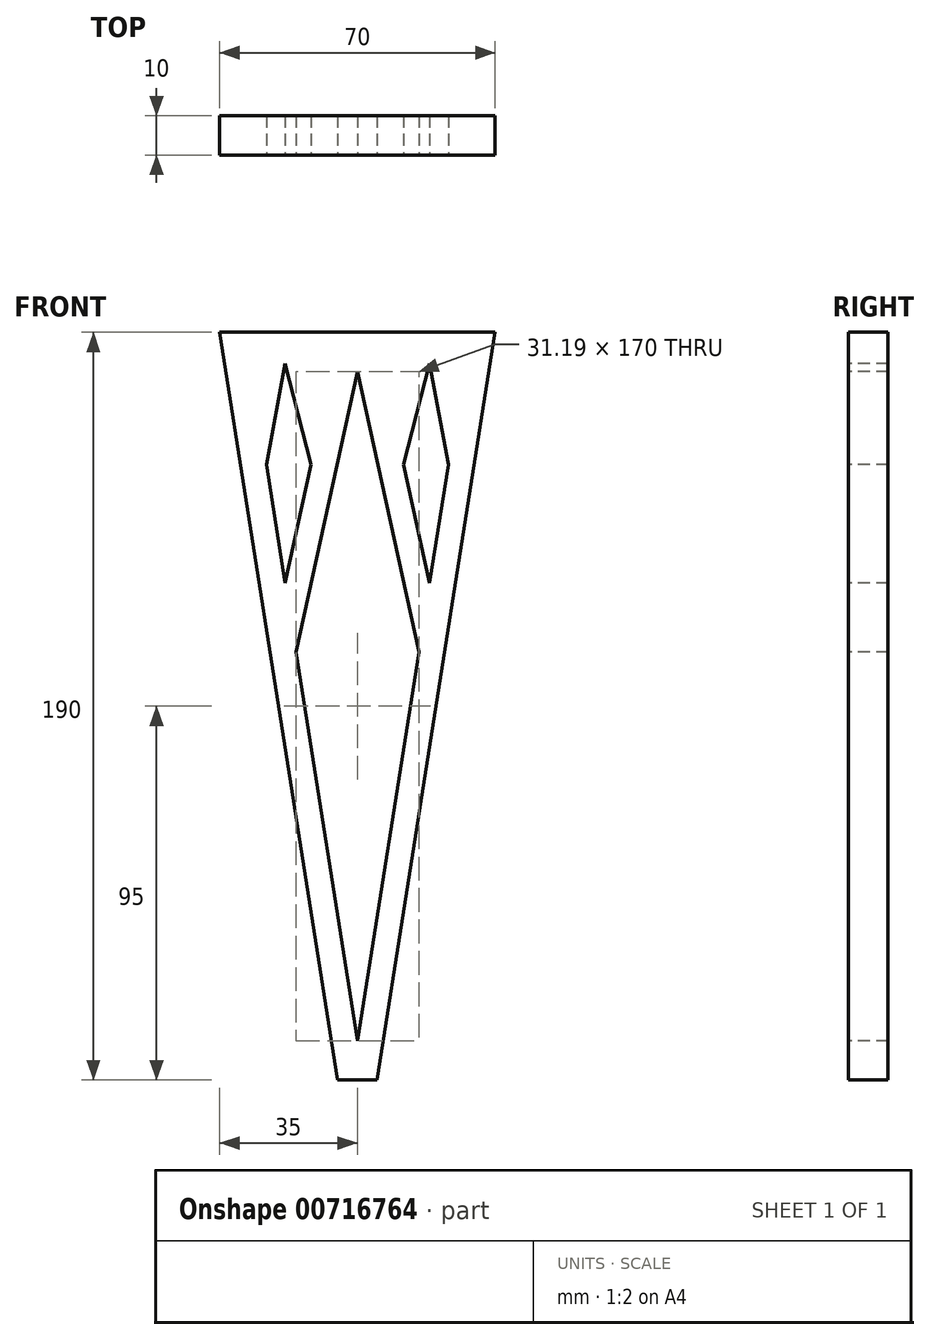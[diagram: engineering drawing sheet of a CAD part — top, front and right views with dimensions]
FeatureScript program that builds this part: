
annotation { "Feature Type Name" : "Feature", "Feature Type Description" : "" }
export const myFeature = defineFeature(function(context is Context, id is Id, definition is map)
    precondition{}
    {
        {
            var Q0;
            Q0=qCreatedBy(makeId("Top.planeOp"),FACE);
            var sketch = newSketch(context, id + "F0", { "sketchPlane" : qUnion([Q0])});
            skLineSegment(sketch, "E0.bottom", {"start": v(0, 0) * mm, "end": v(80, 0) * mm});
            skLineSegment(sketch, "E0.top", {"start": v(0, 16) * mm, "end": v(80, 16) * mm});
            skLineSegment(sketch, "E0.left", {"start": v(0, 0) * mm, "end": v(0, 16) * mm});
            skLineSegment(sketch, "E0.right", {"start": v(80, 0) * mm, "end": v(80, 16) * mm});
            skSolve(sketch);
        }
        {
            var Q0;
            Q0 = qSketchRegion(id + "F0", true);
            extrude(context, id + "F1", {"entities" : qUnion([Q0]), "depth" : 160 * mm, "offsetDistance" : 25 * mm});
        }
        {
            var Q0;
            Q0=makeQuery(id+"F1.opExtrude","SWEPT_FACE",FACE,{"disambiguationData":[OSD([sQuery(id+"F0.wireOp",EDGE,"E0.bottom")])]});
            var sketch = newSketch(context, id + "F2", { "sketchPlane" : qUnion([Q0])});
            skLineSegment(sketch, "E1", {"start": v(0, 0) * mm, "end": v(32.5, 0) * mm});
            skLineSegment(sketch, "E2", {"start": v(32.5, 0) * mm, "end": v(0, 160) * mm});
            skLineSegment(sketch, "E3", {"start": v(0, 160) * mm, "end": v(0, 0) * mm});
            skSolve(sketch);
        }
        {
            var Q0;
            Q0 = qSketchRegion(id + "F2", true);
            extrude(context, id + "F3", {"entities" : qUnion([Q0]), "operationType" : NewBodyOperationType.REMOVE, "oppositeDirection" : true, "depth" : 25 * mm, "offsetDistance" : 25 * mm});
        }
        {
            var Q0;
            Q0=makeQuery(id+"F1.opExtrude","SWEPT_FACE",FACE,{"disambiguationData":[OSD([sQuery(id+"F0.wireOp",EDGE,"E0.bottom")])]});
            var sketch = newSketch(context, id + "F4", { "sketchPlane" : qUnion([Q0])});
            skLineSegment(sketch, "E4", {"start": v(80, 0) * mm, "end": v(47.5, 0) * mm});
            skLineSegment(sketch, "E5", {"start": v(47.5, 0) * mm, "end": v(80, 160) * mm});
            skLineSegment(sketch, "E6", {"start": v(80, 160) * mm, "end": v(80, 0) * mm});
            skSolve(sketch);
        }
        {
            var Q0;
            Q0 = qSketchRegion(id + "F4", true);
            extrude(context, id + "F5", {"entities" : qUnion([Q0]), "operationType" : NewBodyOperationType.REMOVE, "oppositeDirection" : true, "depth" : 25 * mm, "offsetDistance" : 25 * mm});
        }
        {
            var Q0;
            Q0=makeQuery(id+"F1.opExtrude","SWEPT_BODY",BODY,{"disambiguationData":[OSD([sQuery(id+"F0.wireOp",EDGE,"E0.bottom"),sQuery(id+"F0.wireOp",EDGE,"E0.top"),sQuery(id+"F0.wireOp",EDGE,"E0.left"),sQuery(id+"F0.wireOp",EDGE,"E0.right")])]});
            deleteBodies(context, id + "F6", {"entities" : qUnion([Q0])});
        }
        {
            var Q0;
            Q0=qCreatedBy(makeId("Top.planeOp"),FACE);
            var sketch = newSketch(context, id + "F7", { "sketchPlane" : qUnion([Q0])});
            skLineSegment(sketch, "E7.bottom", {"start": v(0, 0) * mm, "end": v(70, 0) * mm});
            skLineSegment(sketch, "E7.top", {"start": v(0, 10) * mm, "end": v(70, 10) * mm});
            skLineSegment(sketch, "E7.left", {"start": v(0, 0) * mm, "end": v(0, 10) * mm});
            skLineSegment(sketch, "E7.right", {"start": v(70, 0) * mm, "end": v(70, 10) * mm});
            skSolve(sketch);
        }
        {
            var Q0;
            Q0 = qSketchRegion(id + "F7", true);
            extrude(context, id + "F8", {"entities" : qUnion([Q0]), "depth" : 190 * mm, "offsetDistance" : 25 * mm});
        }
        {
            var Q0;
            Q0=makeQuery(id+"F8.opExtrude","SWEPT_FACE",FACE,{"disambiguationData":[OSD([sQuery(id+"F7.wireOp",EDGE,"E7.bottom")])]});
            var sketch = newSketch(context, id + "F9", { "sketchPlane" : qUnion([Q0])});
            skLineSegment(sketch, "E8", {"start": v(0, 0) * mm, "end": v(30, 0) * mm});
            skLineSegment(sketch, "E9", {"start": v(30, 0) * mm, "end": v(0, 190) * mm});
            skLineSegment(sketch, "E10", {"start": v(0, 190) * mm, "end": v(0, 0) * mm});
            skSolve(sketch);
        }
        {
            var Q0;
            Q0 = qSketchRegion(id + "F9", true);
            extrude(context, id + "F10", {"entities" : qUnion([Q0]), "operationType" : NewBodyOperationType.REMOVE, "oppositeDirection" : true, "depth" : 25 * mm, "offsetDistance" : 25 * mm});
        }
        {
            var Q0;
            Q0=makeQuery(id+"F8.opExtrude","SWEPT_FACE",FACE,{"disambiguationData":[OSD([sQuery(id+"F7.wireOp",EDGE,"E7.bottom")])]});
            var sketch = newSketch(context, id + "F11", { "sketchPlane" : qUnion([Q0])});
            skLineSegment(sketch, "E11", {"start": v(70, 0) * mm, "end": v(40, 0) * mm});
            skLineSegment(sketch, "E12", {"start": v(40, 0) * mm, "end": v(70, 190) * mm});
            skLineSegment(sketch, "E13", {"start": v(70, 190) * mm, "end": v(70, 0) * mm});
            skSolve(sketch);
        }
        {
            var Q0;
            Q0 = qSketchRegion(id + "F11", true);
            extrude(context, id + "F12", {"entities" : qUnion([Q0]), "operationType" : NewBodyOperationType.REMOVE, "oppositeDirection" : true, "depth" : 25 * mm, "offsetDistance" : 25 * mm});
        }
        {
            var Q0;
            Q0=makeQuery(id+"F8.opExtrude","SWEPT_FACE",FACE,{"disambiguationData":[OSD([sQuery(id+"F7.wireOp",EDGE,"E7.bottom")])]});
            var sketch = newSketch(context, id + "F13", { "sketchPlane" : qUnion([Q0])});
            skLineSegment(sketch, "E14", {"start": v(35, 0) * mm, "end": v(35, 10) * mm});
            skLineSegment(sketch, "E15", {"start": v(35, 10) * mm, "end": v(19.4, 108.78) * mm});
            skLineSegment(sketch, "E16", {"start": v(35, 190) * mm, "end": v(35, 180) * mm});
            skLineSegment(sketch, "E17", {"start": v(19.4, 108.78) * mm, "end": v(35, 180) * mm});
            skLineSegment(sketch, "E18", {"start": v(35, 10) * mm, "end": v(50.6, 108.78) * mm});
            skLineSegment(sketch, "E19", {"start": v(50.6, 108.78) * mm, "end": v(35, 180) * mm});
            skSolve(sketch);
        }
        {
            var Q0;
            Q0=makeQuery(id+"F13.imprint","IMPRINT",FACE,{"disambiguationData":[TD([[makeQuery(id+"F13.imprint","IMPRINT",EDGE,{"derivedFrom":sQuery(id+"F13.wireOp",EDGE,"E15")}),-1.0]])]});
            extrude(context, id + "F14", {"entities" : qUnion([Q0]), "operationType" : NewBodyOperationType.REMOVE, "oppositeDirection" : true, "depth" : 25 * mm, "offsetDistance" : 25 * mm});
        }
        {
            var Q0;
            Q0=makeQuery(id+"F8.opExtrude","SWEPT_FACE",FACE,{"disambiguationData":[OSD([sQuery(id+"F7.wireOp",EDGE,"E7.bottom")])]});
            var sketch = newSketch(context, id + "F15", { "sketchPlane" : qUnion([Q0])});
            skLineSegment(sketch, "E20", {"start": v(16.65, 126.23) * mm, "end": v(11.88, 156.43) * mm});
            skLineSegment(sketch, "E21", {"start": v(17.5, 130.09) * mm, "end": v(23.26, 156.43) * mm});
            skLineSegment(sketch, "E22", {"start": v(17.5, 130.09) * mm, "end": v(16.65, 126.23) * mm});
            skLineSegment(sketch, "E23", {"start": v(11.88, 156.43) * mm, "end": v(16.65, 182) * mm});
            skLineSegment(sketch, "E24", {"start": v(16.65, 182) * mm, "end": v(23.26, 156.43) * mm});
            skPoint(sketch, "E25.start.orphan", {"position": v(16.65, 190) * mm});
            skPoint(sketch, "E26.orphan", {"position": v(7.11, 186.62) * mm});
            skLineSegment(sketch, "E27", {"start": v(35, 190) * mm, "end": v(35, 180) * mm});
            skLineSegment(sketch, "E28.MirrorCS", {"start": v(53.35, 182) * mm, "end": v(46.74, 156.43) * mm});
            skLineSegment(sketch, "E29.MirrorCS", {"start": v(58.12, 156.43) * mm, "end": v(53.35, 182) * mm});
            skLineSegment(sketch, "E30.MirrorCS", {"start": v(52.5, 130.09) * mm, "end": v(46.74, 156.43) * mm});
            skLineSegment(sketch, "E31.MirrorCS", {"start": v(53.35, 126.23) * mm, "end": v(58.12, 156.43) * mm});
            skLineSegment(sketch, "E32.MirrorCS", {"start": v(52.5, 130.09) * mm, "end": v(53.35, 126.23) * mm});
            skSolve(sketch);
        }
        {
            var Q0;
            Q0=makeQuery(id+"F15.imprint","IMPRINT",FACE,{"disambiguationData":[TD([[makeQuery(id+"F15.imprint","IMPRINT",EDGE,{"derivedFrom":sQuery(id+"F15.wireOp",EDGE,"E20")}),-1.0]])]});
            var Q1;
            Q1=makeQuery(id+"F15.imprint","IMPRINT",FACE,{"disambiguationData":[TD([[makeQuery(id+"F15.imprint","IMPRINT",EDGE,{"derivedFrom":sQuery(id+"F15.wireOp",EDGE,"E28.MirrorCS")}),1.0]])]});
            extrude(context, id + "F16", {"entities" : qUnion([Q0, Q1]), "operationType" : NewBodyOperationType.REMOVE, "oppositeDirection" : true, "depth" : 25 * mm, "offsetDistance" : 25 * mm});
        }
    });
